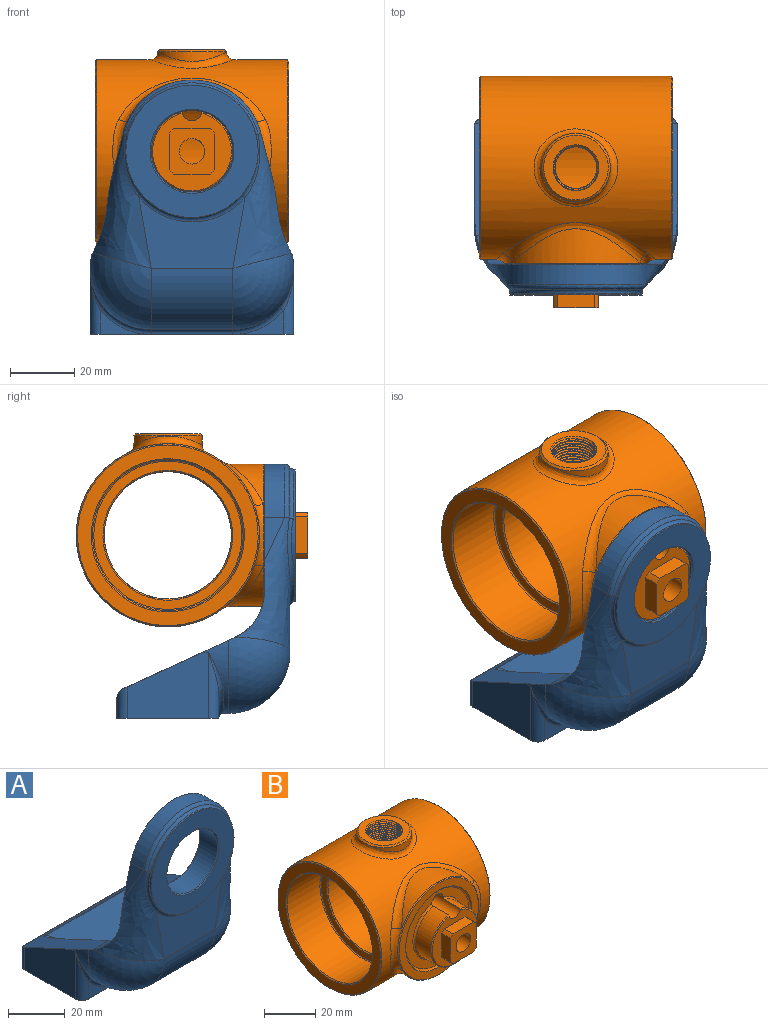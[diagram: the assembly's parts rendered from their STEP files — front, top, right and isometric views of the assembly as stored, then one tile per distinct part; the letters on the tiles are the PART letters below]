
ASSEMBLY  parts=2 mates=1
PART A: 53 faces, bbox 64.2x56.7x83.4 mm
  f0: cylinder r=15.88mm len=17.13mm, axis (-1,0,0), area 170.7mm2, adj f3,f5,f18,f38,f47
  f1: cylinder r=19.05mm len=22.82mm, axis (0,-1,0), area 94.5mm2, adj f6,f9,f14,f34,f35,f38
  f2: cylinder r=19.05mm len=22.82mm, axis (0,-1,0), area 94.5mm2, adj f5,f8,f14,f31,f32,f38
  f3: bspline ~42.44x19.05mm, area 495mm2, adj f0,f5,f11,f16,f17,f18,f22
  f4: bspline ~42.07x19.05mm, area 495mm2, adj f6,f10,f16,f17,f18,f23,f37
  f5: sphere r=19.05mm, area 660.6mm2, adj f0,f2,f3,f15,f38
  f6: sphere r=19.05mm, area 660.6mm2, adj f1,f4,f15,f37,f38
  f7: plane 57.15x6.35mm, normal (0,1,0), area 362.9mm2, adj f26,f27,f29,f36
  f8: plane 25.4x20.64mm, normal (1,0,0), area 397.2mm2, adj f2,f26,f29,f30,f38
  f9: plane 25.4x20.64mm, normal (-1,0,0), area 397.2mm2, adj f1,f26,f27,f28,f38
  f10: plane 13.57x6.35mm, normal (-0.97,0,0.25), area 44.5mm2, adj f4,f12,f18
  f11: plane 13.57x6.35mm, normal (0.97,0,0.25), area 44.5mm2, adj f3,f12,f18
  f12: cylinder r=22.23mm len=43.04mm, axis (0,-1,0), area 372.1mm2, adj f10,f11,f17,f18
  f13: plane 15.88x7.45mm, normal (0,-1,0), area 36.1mm2, adj f26,f28,f34
  f14: plane 25.4x1.59mm, normal (0,0,-1), area 40.3mm2, adj f1,f2,f15,f33
  f15: cylinder r=19.05mm len=25.4mm, axis (-1,0,0), area 760.1mm2, adj f5,f6,f14,f16
  f16: plane 33.07x21.95mm, normal (0,-1,0), area 470.5mm2, adj f3,f4,f15,f24
  f17: revolved ~43.04x16.88mm, area 99.5mm2, adj f3,f4,f12,f21,f22
  f18: plane 59.46x54.01mm, normal (0,1,0), area 1622.2mm2, adj f0,f3,f4,f10,f11,f12,f37,f44
  f19: cylinder r=20.64mm len=41.28mm, axis (0,1,0), area 67.5mm2, adj f20,f21,f22,f23,f24
  f20: plane 41.28x41.28mm, normal (0,-1,0), area 799.2mm2, adj f19,f52
  f21: torus R=22.03mm, axis (0,1,0), area 83.6mm2, adj f17,f19,f22,f23
  f22: bspline ~20.84x5.77mm, area 32.8mm2, adj f3,f17,f19,f21,f24
  f23: bspline ~20.84x5.77mm, area 32.8mm2, adj f4,f19,f21,f24
  f24: torus R=22.03mm, axis (0,1,0), area 78.8mm2, adj f16,f19,f22,f23
  f25: plane 15.88x7.45mm, normal (0,-1,0), area 36.1mm2, adj f26,f30,f32
  f26: plane 63.5x31.75mm, normal (0,0,-1), area 2007.5mm2, adj f7,f8,f9,f13,f25,f27,f28,f29
  f27: cylinder r=3.17mm len=9.84mm, axis (0,0,1), area 41.3mm2, adj f7,f9,f26,f36,f38
  f28: cylinder r=3.17mm len=20.64mm, axis (0,0,-1), area 70mm2, adj f9,f13,f26,f35
  f29: cylinder r=3.17mm len=9.84mm, axis (0,0,-1), area 41.3mm2, adj f7,f8,f26,f36,f38
  f30: cylinder r=3.17mm len=20.64mm, axis (0,0,1), area 70mm2, adj f8,f25,f26,f31
  f31: bspline ~13.5x4.76mm, area 11.4mm2, adj f2,f30,f32
  f32: torus R=20.64mm, axis (0,1,0), area 43mm2, adj f2,f25,f31,f33
  f33: cylinder r=1.59mm len=25.4mm, axis (1,0,0), area 63.3mm2, adj f14,f26,f32,f34
  f34: torus R=20.64mm, axis (0,1,0), area 43mm2, adj f1,f13,f33,f35
  f35: bspline ~13.19x4.76mm, area 11.4mm2, adj f1,f28,f34
  f36: cylinder r=3.17mm len=62.92mm, axis (-1,0,0), area 217.4mm2, adj f7,f27,f29,f38
  f37: cylinder r=15.88mm len=17.13mm, axis (-1,0,0), area 170.7mm2, adj f4,f6,f18,f38,f48
  f38: plane 63.54x34.97mm, normal (0,0.42,0.91), area 697.2mm2, adj f0,f1,f2,f5,f6,f8,f9,f27
  f39: cylinder r=12.7mm len=25.4mm, axis (0,1,0), area 696.7mm2, adj f51,f52
  f40: plane 44.05x0.32mm, normal (0,-1,0), area 13.7mm2, adj f38,f41,f42,f43
  f41: bspline ~31.75x13.89mm, area 367.4mm2, adj f38,f40,f42,f45,f49
  f42: plane 41.28x31.75mm, normal (0,0,1), area 1058.5mm2, adj f40,f41,f43,f44
  f43: bspline ~31.75x13.89mm, area 367.4mm2, adj f38,f40,f42,f46,f50
  f44: cylinder r=11.11mm len=25.4mm, axis (1,0,0), area 443.4mm2, adj f18,f42,f45,f46
  f45: sphere r=11.11mm, area 225.2mm2, adj f41,f44,f47
  f46: sphere r=11.11mm, area 225.2mm2, adj f43,f44,f48
  f47: bspline ~21.08x11.11mm, area 135.7mm2, adj f0,f18,f38,f45,f49
  f48: bspline ~21.08x11.11mm, area 135.7mm2, adj f18,f37,f38,f46,f50
  f49: bspline ~6.96x3.19mm, area 3.4mm2, adj f38,f41,f47
  f50: bspline ~48.81x38.1mm, area 3.4mm2, adj f38,f43,f48
  f51: cone r=12.7mm half-angle=45deg, axis (0,1,0), area 45.5mm2, adj f18,f39
  f52: cone r=13.1mm half-angle=45deg, axis (0,-1,0), area 45.5mm2, adj f20,f39
PART B: 60 faces, bbox 60.3x72.2x60.6 mm
  f0: cylinder r=19.84mm len=39.69mm, axis (1,0,0), area 2508.3mm2, adj f4,f5,f25,f26,f46,f48,f49,f50
  f1: cylinder r=12.7mm len=25.4mm, axis (0,1,0), area 612mm2, adj f2,f3,f59
  f2: cone r=12.7mm half-angle=45deg, axis (0,1,0), area 40.6mm2, adj f1,f8,f59
  f3: torus R=13.49mm, axis (0,1,0), area 93.9mm2, adj f1,f17,f59
  f4: cylinder r=6.51mm len=13.02mm, axis (0,0,-1), area -12.2mm2, adj f0,f7,f52,f53,f57
  f5: cylinder r=6.51mm len=9.23mm, axis (0,0,-1), area 0mm2, adj f0,f51
  f6: cone r=7.14mm half-angle=45deg, axis (0,0,1), area 15.5mm2, adj f7,f13,f53,f54,f55
  f7: cone r=7.14mm half-angle=45deg, axis (0,0,1), area 4.2mm2, adj f4,f6,f53,f56,f57
  f8: plane 24.61x24.22mm, normal (0,-1,0), area 262.7mm2, adj f2,f37,f38,f39,f40,f41,f42,f43
  f9: cylinder r=22.23mm len=40.02mm, axis (0,1,0), area 303.3mm2, adj f28,f34
  f10: cylinder r=28.57mm len=59.53mm, axis (-1,0,0), area 8169.1mm2, adj f22,f27,f32,f33,f34,f35,f36
  f11: plane 56.36x56.36mm, normal (-1,0,0), area 700.8mm2, adj f22,f24
  f12: plane 56.36x56.36mm, normal (1,0,0), area 700.8mm2, adj f23,f27
  f13: plane 20.16x20.16mm, normal (0,0,1), area 158.9mm2, adj f6,f47
  f14: cylinder r=10.72mm len=21.43mm, axis (0,0,1), area 107.3mm2, adj f32,f47
  f15: cylinder r=22.23mm len=40.02mm, axis (0,1,0), area 303.3mm2, adj f28,f35
  f16: plane 43.66x43.66mm, normal (0,-1,0), area 449.8mm2, adj f28,f29
  f17: plane 34.93x34.93mm, normal (0,-1,0), area 374.4mm2, adj f3,f29,f59
  f18: cylinder r=23.5mm len=47mm, axis (1,0,0), area 2654.1mm2, adj f24,f31
  f19: cylinder r=23.5mm len=47mm, axis (1,0,0), area 2654.1mm2, adj f23,f30
  f20: plane 46.2x46.2mm, normal (1,0,0), area 389.4mm2, adj f26,f30
  f21: plane 46.2x46.2mm, normal (-1,0,0), area 389.4mm2, adj f25,f31
  f22: cone r=28.18mm half-angle=45deg, axis (1,0,0), area 100.1mm2, adj f10,f11
  f23: cone r=23.5mm half-angle=45deg, axis (1,0,0), area 83.6mm2, adj f12,f19
  f24: cone r=23.89mm half-angle=45deg, axis (-1,0,0), area 83.6mm2, adj f11,f18
  f25: cone r=20.24mm half-angle=45deg, axis (-1,0,0), area 70.7mm2, adj f0,f21
  f26: cone r=19.84mm half-angle=45deg, axis (1,0,0), area 70.7mm2, adj f0,f20
  f27: cone r=28.57mm half-angle=45deg, axis (-1,0,0), area 100.1mm2, adj f10,f12
  f28: cone r=22.23mm half-angle=45deg, axis (0,1,0), area 77.7mm2, adj f9,f15,f16,f33,f36
  f29: torus R=17.46mm, axis (0,1,0), area 140.8mm2, adj f16,f17
  f30: torus R=23.1mm, axis (1,0,0), area 91.5mm2, adj f19,f20
  f31: torus R=23.1mm, axis (-1,0,0), area 91.5mm2, adj f18,f21
  f32: bspline ~26.21x24.2mm, area 233.1mm2, adj f10,f14
  f33: bspline ~22.39x5.46mm, area 68.5mm2, adj f10,f28,f34,f35
  f34: bspline ~47.1x15.42mm, area 175.1mm2, adj f9,f10,f33,f36
  f35: bspline ~45.74x13.46mm, area 175.1mm2, adj f10,f15,f33,f36
  f36: bspline ~22.39x5.46mm, area 68.5mm2, adj f10,f28,f34,f35
  f37: plane 11.42x4.76mm, normal (0,0,1), area 54.4mm2, adj f8,f38,f44,f45
  f38: cylinder r=9.14mm len=4.76mm, axis (0,1,0), area 9.7mm2, adj f8,f37,f39,f45
  f39: plane 11.42x4.76mm, normal (-1,0,0), area 54.4mm2, adj f8,f38,f40,f45
  f40: cylinder r=9.14mm len=4.76mm, axis (0,1,0), area 9.7mm2, adj f8,f39,f41,f45
  f41: plane 11.42x4.76mm, normal (0,0,-1), area 54.4mm2, adj f8,f40,f42,f45
  f42: cylinder r=9.14mm len=4.76mm, axis (0,1,0), area 9.7mm2, adj f8,f41,f43,f45
  f43: plane 11.42x4.76mm, normal (1,0,0), area 54.4mm2, adj f8,f42,f44,f45
  f44: cylinder r=9.14mm len=4.76mm, axis (0,1,0), area 9.7mm2, adj f8,f37,f43,f45
  f45: plane 14.29x14.29mm, normal (0,-1,0), area 150.8mm2, adj f37,f38,f39,f40,f41,f42,f43,f44
  f46: cylinder r=6.51mm len=3.14mm, axis (0,0,-1), area 0mm2, adj f0,f50
  f47: cone r=10.08mm half-angle=45deg, axis (0,0,-1), area 58.7mm2, adj f13,f14
  f48: bspline ~10.76x8.29mm, area 2.7mm2, adj f0,f49,f52,f54
  f49: bspline ~10.61x8.17mm, area 4.1mm2, adj f0,f48,f50,f52
  f50: bspline ~6.58x1.96mm, area 0.6mm2, adj f0,f46,f49
  f51: bspline ~13.15x7.59mm, area 1.5mm2, adj f0,f5,f56
  f52: plane 0.85x0.6mm, normal (-0.93,0.38,0), area 0.3mm2, adj f0,f4,f48,f49,f53,f54
  f53: bspline ~15.19x13.15mm, area 66.9mm2, adj f4,f6,f7,f52,f54
  f54: bspline ~16.33x14.14mm, area 290.8mm2, adj f0,f6,f48,f52,f53,f55
  f55: bspline ~16.57x14.35mm, area 153.5mm2, adj f0,f6,f54,f56
  f56: bspline ~16.33x14.14mm, area 295.2mm2, adj f0,f7,f51,f55,f57
  f57: bspline ~15.19x13.15mm, area 66.7mm2, adj f0,f4,f7,f56
  f58: cylinder r=3.97mm len=24.21mm, axis (0,1,0), area 603.8mm2, adj f0,f45
  f59: cylinder r=3.17mm len=26.99mm, axis (0,1,0), area 375.4mm2, adj f0,f1,f2,f3,f8,f17
PLACE A t=(24.23,30.39,3.77)mm fixed
PLACE B rot(axis=(0,1,0),0deg) t=(24.23,49.44,40.28)mm
MATE revolute B.f1 <-> A.f12  axis (0,-1,0) through (24.23,19.28,40.28)mm
